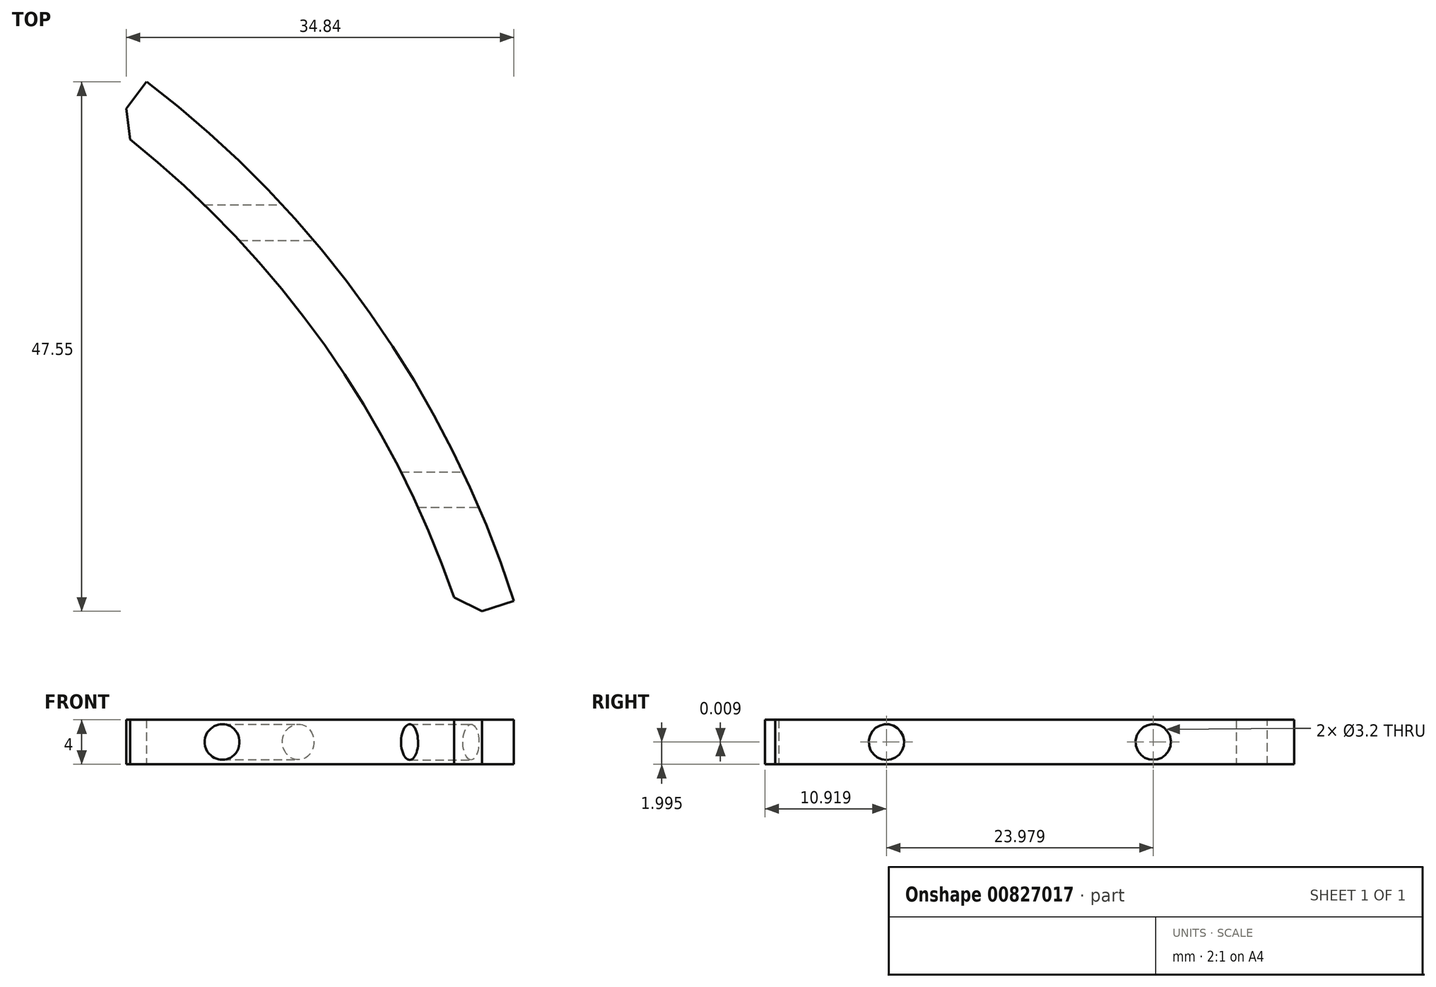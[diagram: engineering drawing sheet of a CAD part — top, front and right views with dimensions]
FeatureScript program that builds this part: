
annotation { "Feature Type Name" : "Feature", "Feature Type Description" : "" }
export const myFeature = defineFeature(function(context is Context, id is Id, definition is map)
    precondition{}
    {
        {
            var Q0;
            Q0=qCreatedBy(makeId("Top.planeOp"),FACE);
            var sketch = newSketch(context, id + "F0", { "sketchPlane" : qUnion([Q0])});
            skLineSegment(sketch, "E0", {"start": v(-73.46, 52) * mm, "end": v(73.46, 52) * mm, "construction": true});
            skLineSegment(sketch, "E1", {"start": v(0, 0) * mm, "end": v(0, 90) * mm, "construction": true});
            skCircle(sketch, "E2", {"center": v(0, 52) * mm, "radius": 14 * mm, "construction": true});
            skLineSegment(sketch, "E3.MirrorCS", {"start": v(-73.46, 84) * mm, "end": v(73.46, 84) * mm, "construction": true});
            skArc(sketch, "E4", {"start": v(85.7, 27.5) * mm, "mid": v(73.46, 52) * mm, "end": v(54.42, 71.68) * mm});
            skArc(sketch, "E5", {"start": v(90.46, 29.03) * mm, "mid": v(77.54, 54.89) * mm, "end": v(57.44, 75.66) * mm});
            skLineSegment(sketch, "E6", {"start": v(54.42, 71.68) * mm, "end": v(57.44, 75.66) * mm});
            skLineSegment(sketch, "E7", {"start": v(85.7, 27.5) * mm, "end": v(90.46, 29.03) * mm});
            skCircle(sketch, "E8", {"center": v(0, 0) * mm, "radius": 90 * mm, "construction": true});
            skLineSegment(sketch, "E9", {"start": v(73.46, 52) * mm, "end": v(0, 0) * mm, "construction": true});
            skSolve(sketch);
        }
        {
            var Q0;
            Q0 = qSketchRegion(id + "F0", true);
            extrude(context, id + "F1", {"entities" : qUnion([Q0]), "depth" : 4 * mm, "offsetDistance" : 25 * mm});
        }
        {
            var Q0;
            Q0=qCreatedBy(makeId("Right.planeOp"),FACE);
            cPlane(context, id + "F2", {"entities" : qUnion([Q0]), "cplaneType" : CPlaneType.OFFSET, "offset" : 90.46 * mm, "width" : 150 * mm, "height" : 150 * mm});
        }
        {
            var Q0;
            Q0=qCreatedBy(id+"F2.planeOp",FACE);
            var sketch = newSketch(context, id + "F3", { "sketchPlane" : qUnion([Q0])});
            skPoint(sketch, "E10", {"position": v(39.03, 2) * mm});
            skPoint(sketch, "E11", {"position": v(63, 2) * mm});
            skSolve(sketch);
        }
        {
            var Q0;
            Q0=sQuery(id+"F3.wireOp",VERTEX,"E10");
            var Q1;
            Q1=sQuery(id+"F3.wireOp",VERTEX,"E11");
            var Q2;
            Q2=makeQuery(id+"F1.opExtrude","SWEPT_BODY",BODY,{"disambiguationData":[OSD([sQuery(id+"F0.wireOp",EDGE,"E4"),sQuery(id+"F0.wireOp",EDGE,"E5"),sQuery(id+"F0.wireOp",EDGE,"E6"),sQuery(id+"F0.wireOp",EDGE,"E7")])]});
            hole(context, id + "F4", {"style" : HoleStyle.SIMPLE, "endStyle" : HoleEndStyle.THROUGH, "holeDiameter" : 3.2 * mm, "majorDiameter" : 5 * mm, "isTappedThrough" : true, "tappedDepth" : 12 * mm, "tapClearance" : 3, "startFromSketch" : true, "locations" : qUnion([Q0, Q1]), "scope" : qUnion([Q2])});
        }
        {
            var Q0;
            Q0=makeQuery(id+"F1.opExtrude","SWEPT_EDGE",EDGE,{"disambiguationData":[OSD([sQuery(id+"F0.wireOp",EDGE,"E4"),sQuery(id+"F0.wireOp",EDGE,"E7")])]});
            var Q1;
            Q1=makeQuery(id+"F1.opExtrude","SWEPT_EDGE",EDGE,{"disambiguationData":[OSD([sQuery(id+"F0.wireOp",EDGE,"E4"),sQuery(id+"F0.wireOp",EDGE,"E6")])]});
            chamfer(context, id + "F5", {"entities" : qUnion([Q0, Q1]), "width" : 2 * mm, "tangentPropagation" : true});
        }
    });
